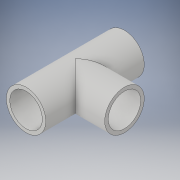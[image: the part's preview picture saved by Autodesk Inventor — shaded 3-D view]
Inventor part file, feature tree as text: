
AUTODESK INVENTOR PART (.ipt)
format: ipt  version: 2018 (Build 220112000, 112)  size: 148,480 bytes
history: native  units: in
note: dims shown in document units (in); Inventor stores cm internally (conversion verified against a paired STEP export)
features: sketch x9, extrude x8, plane x1
ambient origin geometry x8: Origin, YZ Plane, XZ Plane, XY Plane, X Axis, Y Axis, Z Axis, Center Point
bodies: Solid1 (feature_tree)
feature tree (18):
  extrude  "Extrusion1"  Depth=4.0in TaperAngle=0.0deg
  sketch  "Sketch2"  dims[d3=1.1975in d4=0.0in d5=0.8025in d6=0.0in]
  sketch  "Sketch3"  dims[d7=1.321in d8=1.0in]
  plane  "Work Plane1"
  sketch  "Sketch4"  dims[d9=1.321in d10=1.0in]
  extrude  "Extrusion2"  Depth=0.8025in TaperAngle=0.0deg
  extrude  "Extrusion3"  Depth=1.0in
  sketch  "Sketch5"  dims[d11=1.321in d12=1.25in d13=0.0in]
  sketch  "Sketch6"  dims[d14=1.25in d15=0.0in d16=1.25in d17=0.0in]
  sketch  "Sketch7"  dims[d18=4.0in d19=0.0in d20=2.0in d21=0.0in]
  sketch  "Sketch8"
  extrude  "Extrusion4"  Depth=1.0in
  extrude  "Extrusion5"  Depth=1.25in TaperAngle=0.0deg
  extrude  "Extrusion6"  Depth=1.25in TaperAngle=0.0deg
  extrude  "Extrusion7"  Depth=4.0in TaperAngle=0.0deg
  extrude  "Extrusion8"  [1 undecoded]
  sketch  "Sketch1"  dims[d0=1.605in d1=4.0in d2=0.0in]
  sketch  "Sketch9"
note: 1 required parameter value undecoded (feature->parameter linkage not recoverable at this tier; creation-order binding heuristic only, values carry confidence <= 0.55)
